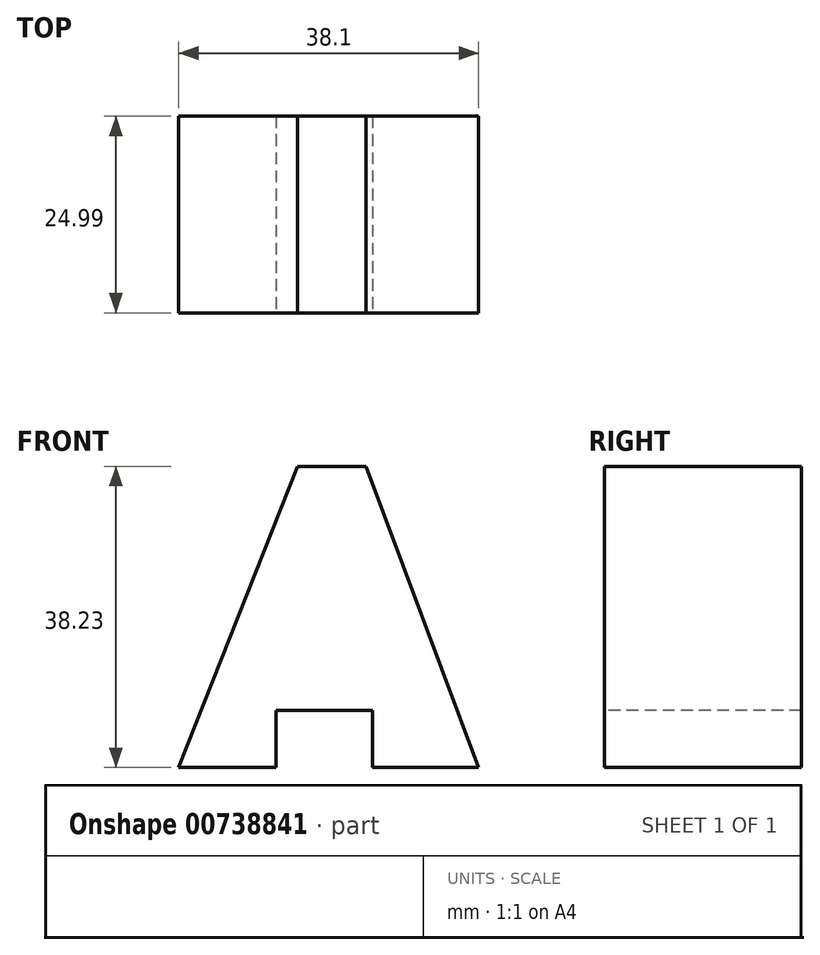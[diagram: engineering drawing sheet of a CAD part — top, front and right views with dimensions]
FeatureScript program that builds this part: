
annotation { "Feature Type Name" : "Feature", "Feature Type Description" : "" }
export const myFeature = defineFeature(function(context is Context, id is Id, definition is map)
    precondition{}
    {
        {
            var Q0;
            Q0=qCreatedBy(makeId("Right.planeOp"),FACE);
            var sketch = newSketch(context, id + "F0", { "sketchPlane" : qUnion([Q0])});
            skLineSegment(sketch, "E0", {"start": v(0, 0) * mm, "end": v(25, 0) * mm});
            skLineSegment(sketch, "E1", {"start": v(25, 0) * mm, "end": v(25, 38.23) * mm});
            skLineSegment(sketch, "E2", {"start": v(25, 38.23) * mm, "end": v(0, 38.23) * mm});
            skLineSegment(sketch, "E3", {"start": v(0, 38.23) * mm, "end": v(0, 0) * mm});
            skSolve(sketch);
        }
        {
            var Q0;
            Q0=makeQuery(id+"F0.imprint","IMPRINT",FACE,{"disambiguationData":[TD([[makeQuery(id+"F0.imprint","IMPRINT",EDGE,{"derivedFrom":sQuery(id+"F0.wireOp",EDGE,"E0")}),1.0]])]});
            extrude(context, id + "F1", {"entities" : qUnion([Q0]), "depth" : 38.1 * mm, "offsetDistance" : 25.4 * mm});
        }
        {
            var Q0;
            Q0=makeQuery(id+"F1.opExtrude","SWEPT_FACE",FACE,{"disambiguationData":[OSD([sQuery(id+"F0.wireOp",EDGE,"E3")])]});
            var sketch = newSketch(context, id + "F2", { "sketchPlane" : qUnion([Q0])});
            skLineSegment(sketch, "E4", {"start": v(12.35, 0) * mm, "end": v(12.35, 7.21) * mm});
            skLineSegment(sketch, "E5", {"start": v(12.35, 7.21) * mm, "end": v(24.6, 7.21) * mm});
            skLineSegment(sketch, "E6", {"start": v(24.6, 7.21) * mm, "end": v(24.6, 0) * mm});
            skLineSegment(sketch, "E7", {"start": v(24.6, 0) * mm, "end": v(12.35, 0) * mm});
            skSolve(sketch);
        }
        {
            var Q0;
            Q0=makeQuery(id+"F2.imprint","IMPRINT",FACE,{"disambiguationData":[TD([[makeQuery(id+"F2.imprint","IMPRINT",EDGE,{"derivedFrom":sQuery(id+"F2.wireOp",EDGE,"E4")}),-1.0]])]});
            extrude(context, id + "F3", {"entities" : qUnion([Q0]), "operationType" : NewBodyOperationType.REMOVE, "endBound" : BoundingType.THROUGH_ALL, "oppositeDirection" : true, "depth" : 25.4 * mm, "offsetDistance" : 25.4 * mm});
        }
        {
            var Q0;
            Q0=makeQuery(id+"F1.opExtrude","SWEPT_FACE",FACE,{"disambiguationData":[OSD([sQuery(id+"F0.wireOp",EDGE,"E3")])]});
            var sketch = newSketch(context, id + "F4", { "sketchPlane" : qUnion([Q0])});
            skLineSegment(sketch, "E8", {"start": v(15.11, 38.23) * mm, "end": v(0, 0) * mm});
            skLineSegment(sketch, "E9", {"start": v(23.8, 38.23) * mm, "end": v(38.1, 0) * mm});
            skSolve(sketch);
        }
        {
            var Q0;
            {var subQ0=sQuery(id+"F4.wireOp",EDGE,"E8");Q0=makeQuery(id+"F4.imprint","IMPRINT",FACE,{"disambiguationData":[TD([[makeQuery(id+"F4.imprint","IMPRINT",EDGE,{"derivedFrom":subQ0}),-1.0]])]});}
            var Q1;
            {var subQ0=sQuery(id+"F4.wireOp",EDGE,"E9");Q1=makeQuery(id+"F4.imprint","IMPRINT",FACE,{"disambiguationData":[TD([[makeQuery(id+"F4.imprint","IMPRINT",EDGE,{"derivedFrom":subQ0}),1.0]])]});}
            extrude(context, id + "F5", {"entities" : qUnion([Q0, Q1]), "operationType" : NewBodyOperationType.REMOVE, "endBound" : BoundingType.THROUGH_ALL, "oppositeDirection" : true, "depth" : 25.4 * mm, "offsetDistance" : 25.4 * mm});
        }
    });
